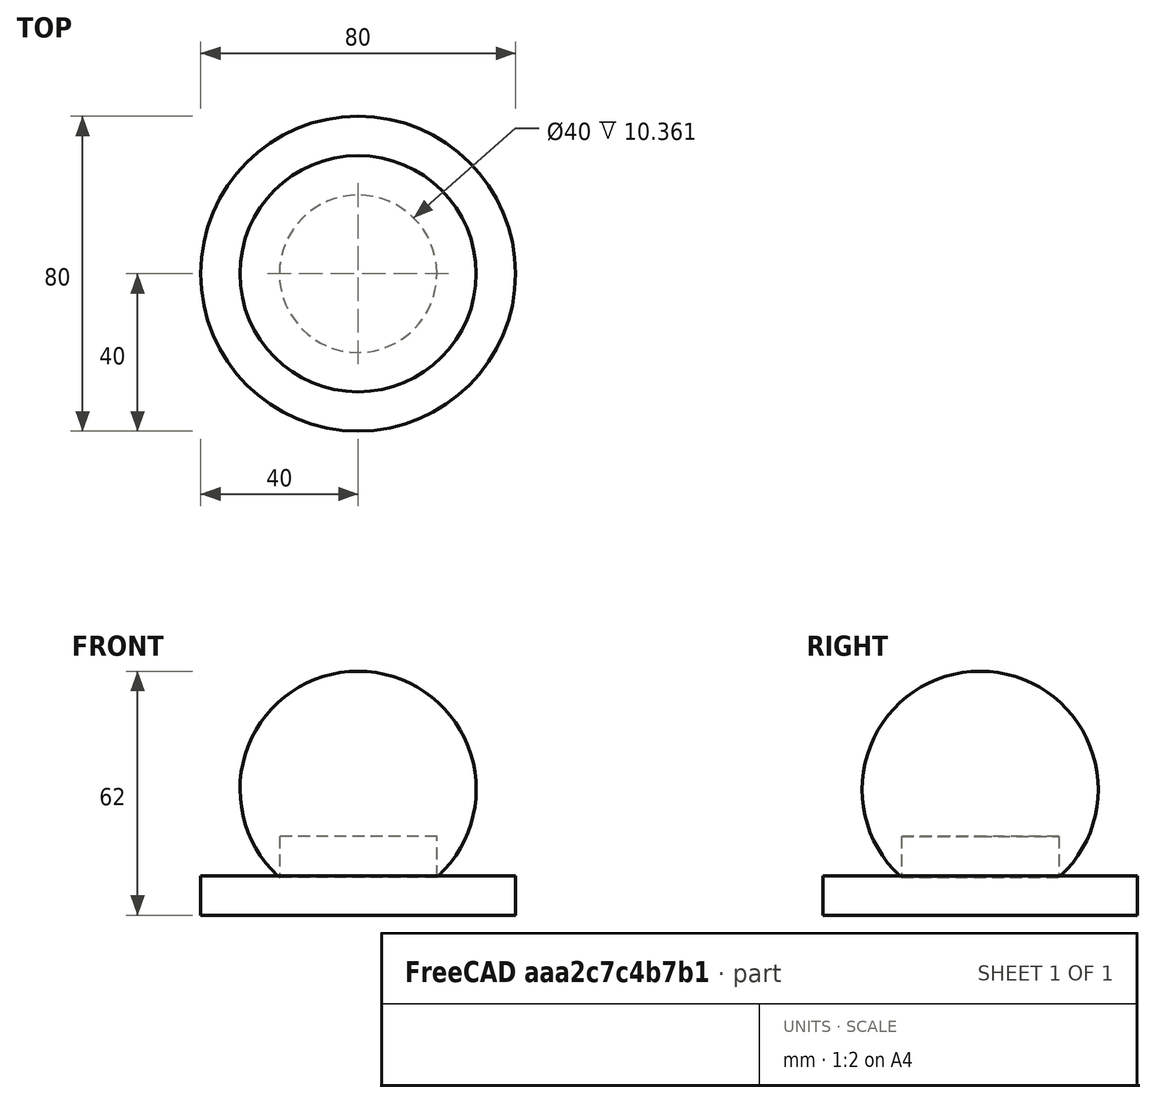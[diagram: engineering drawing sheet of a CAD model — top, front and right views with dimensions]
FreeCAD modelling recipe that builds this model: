
FCSTD DOCUMENT  (FreeCAD 0.20R29410 (Git))
Label: flag pole end
License: All rights reserved
LicenseURL: http://en.wikipedia.org/wiki/All_rights_reserved
objects: Part::Cylinder×2, Part::Sphere×1, Part::Cut×1, App::Part×1
note: 4 computed .brp shape members not serialized (recipe doc carries the construction recipe); baked Part::Feature solids carry a one-line shape summary decoded from their .brp

FEATURE [Part::Sphere] Sphere
  Angle1 = -90
  Angle2 = 90
  Angle3 = 360
  AttacherType = Attacher::AttachEngine3D
  Placement = pos=(0,0,30) rot=(0,0,1;0rad)
  Radius = 30
FEATURE [Part::Cylinder] Cylinder
  Angle = 360
  AttacherType = Attacher::AttachEngine3D
  FirstAngle = 0
  Height = 40
  Placement = pos=(0,0,-22) rot=(0,0,1;0rad)
  Radius = 20
  SecondAngle = 0
FEATURE [Part::Cut] Cut
  Base = -> Sphere
  Tool = -> Cylinder
FEATURE [App::Part] Part
  Group = -> [Sphere,Cylinder,Cut]
  Origin = -> Origin
FEATURE [Part::Cylinder] Cylinder001
  Angle = 360
  AttacherType = Attacher::AttachEngine3D
  FirstAngle = 0
  Height = 10
  Placement = pos=(0,0,-2) rot=(0,0,1;0rad)
  Radius = 40
  SecondAngle = 0
